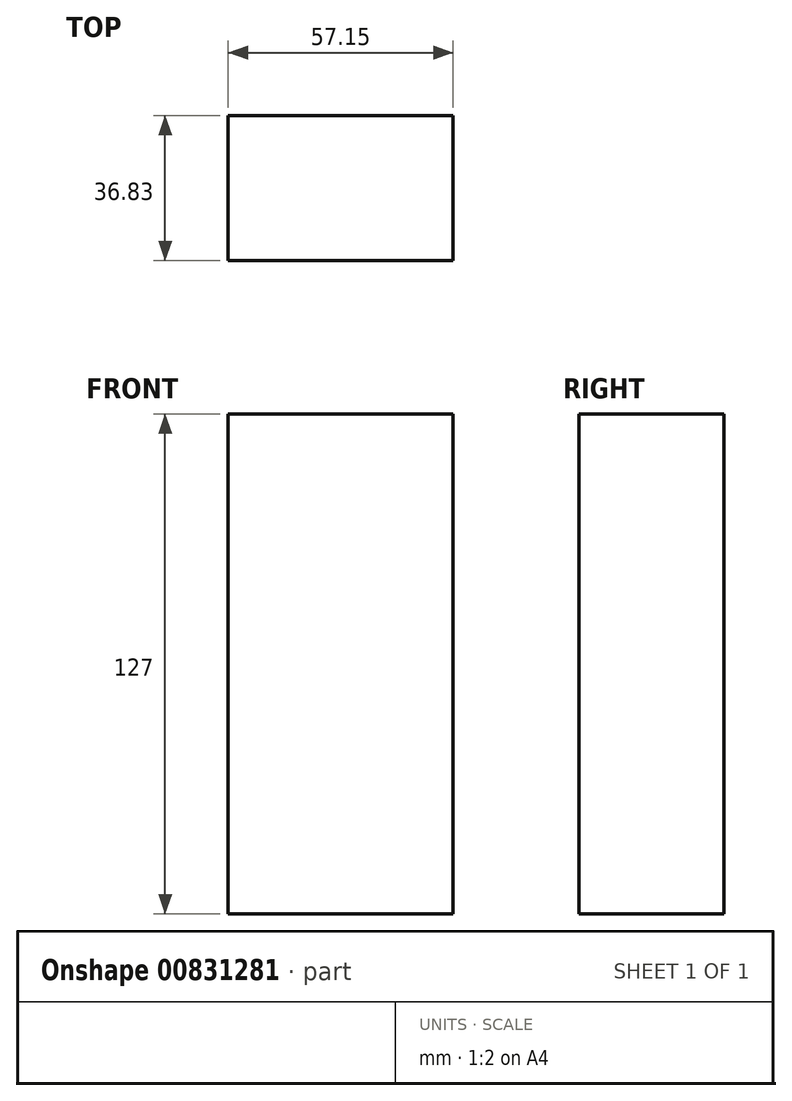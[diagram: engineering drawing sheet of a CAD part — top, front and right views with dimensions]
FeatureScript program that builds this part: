
annotation { "Feature Type Name" : "Feature", "Feature Type Description" : "" }
export const myFeature = defineFeature(function(context is Context, id is Id, definition is map)
    precondition{}
    {
        {
            var Q0;
            Q0=qCreatedBy(makeId("Top.planeOp"),FACE);
            var sketch = newSketch(context, id + "F0", { "sketchPlane" : qUnion([Q0])});
            skLineSegment(sketch, "E0.bottom", {"start": v(-12.43, 9.27) * mm, "end": v(44.72, 9.27) * mm});
            skLineSegment(sketch, "E0.top", {"start": v(-12.43, -27.56) * mm, "end": v(44.72, -27.56) * mm});
            skLineSegment(sketch, "E0.left", {"start": v(-12.43, 9.27) * mm, "end": v(-12.43, -27.56) * mm});
            skLineSegment(sketch, "E0.right", {"start": v(44.72, 9.27) * mm, "end": v(44.72, -27.56) * mm});
            skSolve(sketch);
        }
        {
            var Q0;
            Q0 = qSketchRegion(id + "F0", true);
            extrude(context, id + "F1", {"entities" : qUnion([Q0]), "depth" : 127 * mm, "offsetDistance" : 25.4 * mm});
        }
    });
